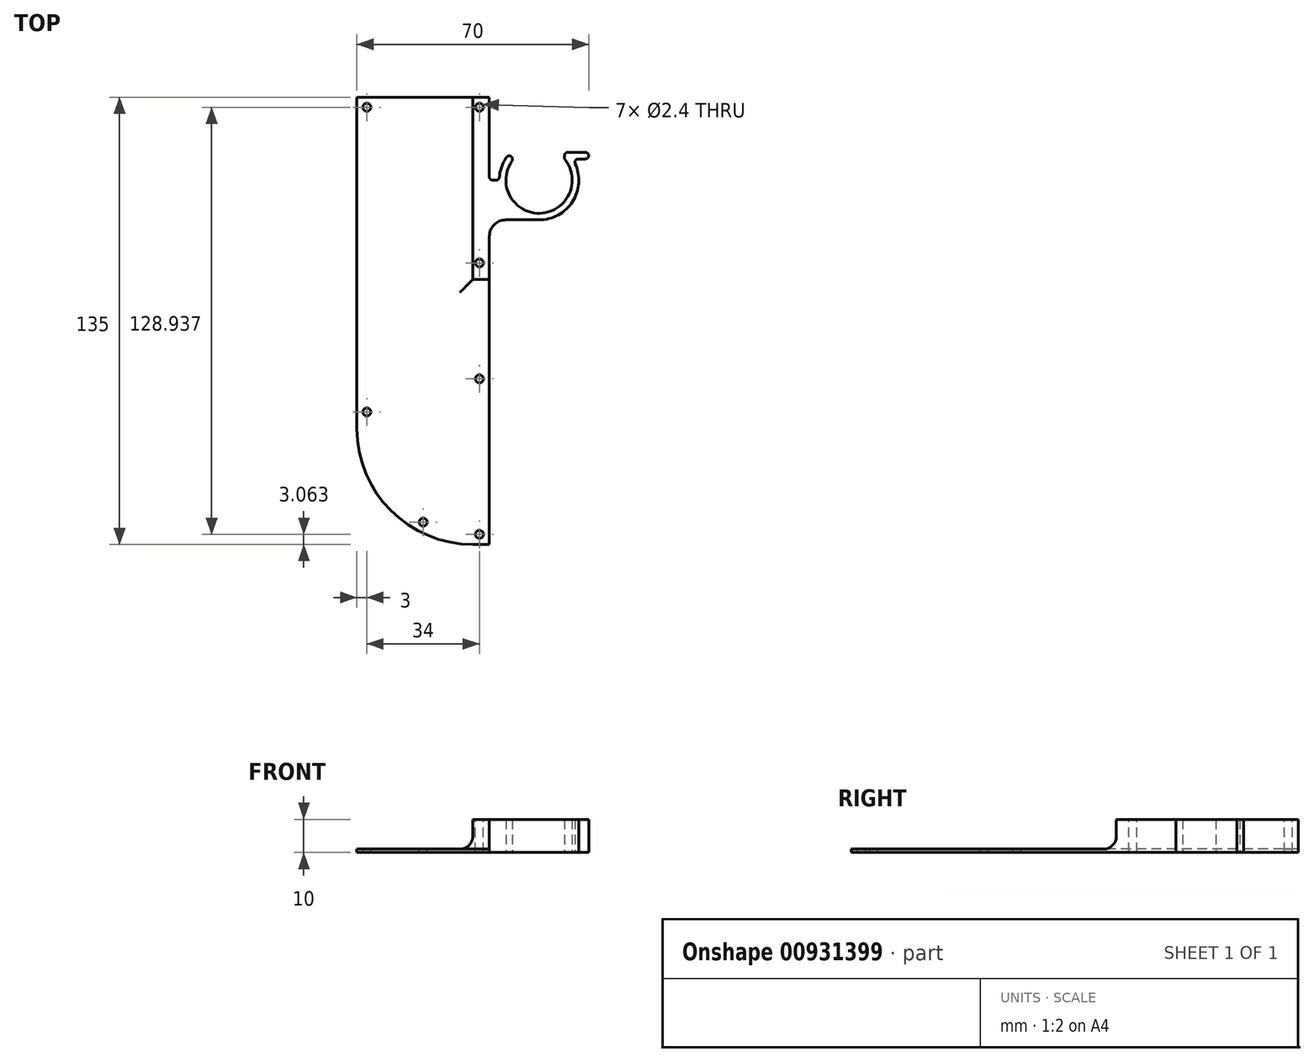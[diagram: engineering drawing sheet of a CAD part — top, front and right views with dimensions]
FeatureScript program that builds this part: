
annotation { "Feature Type Name" : "Feature", "Feature Type Description" : "" }
export const myFeature = defineFeature(function(context is Context, id is Id, definition is map)
    precondition{}
    {
        {
            var Q0;
            Q0=qCreatedBy(makeId("Top.planeOp"),FACE);
            var sketch = newSketch(context, id + "F0", { "sketchPlane" : qUnion([Q0])});
            skLineSegment(sketch, "E0.right", {"start": v(-70, 0) * mm, "end": v(-70, -100) * mm});
            skPoint(sketch, "E1.visualSharp", {"position": v(-70, -135) * mm});
            skArc(sketch, "E1.filletArc", {"start": v(-70, -100) * mm, "mid": v(-59.75, -124.75) * mm, "end": v(-35, -135) * mm});
            skArc(sketch, "E2", {"start": v(-23.18, -19.25) * mm, "mid": v(-14.76, -35) * mm, "end": v(-7.1, -18.86) * mm});
            skPoint(sketch, "E3.visualSharp", {"position": v(-23, -19) * mm});
            skPoint(sketch, "E0.top.start.orphan", {"position": v(0, -135) * mm});
            skPoint(sketch, "E4.visualSharp", {"position": v(-35, -45) * mm});
            skLineSegment(sketch, "E5", {"start": v(-35, -135) * mm, "end": v(-30, -135) * mm});
            skArc(sketch, "E6.0", {"start": v(-15, -37) * mm, "mid": v(-4.9, -31.49) * mm, "end": v(-4.08, -20.02) * mm});
            skLineSegment(sketch, "E7", {"start": v(-30, -135) * mm, "end": v(-30, -42) * mm});
            skLineSegment(sketch, "E8", {"start": v(-25, -37) * mm, "end": v(-15, -37) * mm});
            skPoint(sketch, "E8.endSnap0", {"position": v(-15, -37) * mm});
            skLineSegment(sketch, "E9", {"start": v(-70, 0) * mm, "end": v(-30, 0) * mm});
            skLineSegment(sketch, "E10", {"start": v(-7.18, -17.33) * mm, "end": v(-7.18, -17.33) * mm});
            skPoint(sketch, "E11.visualSharp", {"position": v(-7.86, -18) * mm});
            skPoint(sketch, "E12.visualSharp", {"position": v(-6.43, -16.6) * mm});
            skPoint(sketch, "E13.visualSharp", {"position": v(-30, -37) * mm});
            skArc(sketch, "E13.filletArc", {"start": v(-25, -37) * mm, "mid": v(-28.54, -38.46) * mm, "end": v(-30, -42) * mm});
            skArc(sketch, "E14.0", {"start": v(-24.82, -18.1) * mm, "mid": v(-26.3, -20.94) * mm, "end": v(-26.96, -24.08) * mm});
            skLineSegment(sketch, "E15.top", {"start": v(-27.96, -25) * mm, "end": v(-29, -25) * mm});
            skLineSegment(sketch, "E15.right", {"start": v(-30, 0) * mm, "end": v(-30, -24) * mm});
            skLineSegment(sketch, "E16", {"start": v(-23, -18.68) * mm, "end": v(-23, -18.68) * mm});
            skPoint(sketch, "E15.bottom.start.orphan", {"position": v(-23, 0) * mm});
            skPoint(sketch, "E17.visualSharp", {"position": v(-30, -25) * mm});
            skArc(sketch, "E17.filletArc", {"start": v(-30, -24) * mm, "mid": v(-29.7, -24.7) * mm, "end": v(-29, -25) * mm});
            skArc(sketch, "E18.filletArc", {"start": v(-27.96, -25) * mm, "mid": v(-27.28, -24.73) * mm, "end": v(-26.96, -24.08) * mm});
            skPoint(sketch, "E19.visualSharp", {"position": v(-23, -16.06) * mm});
            skArc(sketch, "E19.filletArc", {"start": v(-23, -18.68) * mm, "mid": v(-23.7, -17.72) * mm, "end": v(-24.82, -18.1) * mm});
            skArc(sketch, "E20.filletArc", {"start": v(-23.18, -19.25) * mm, "mid": v(-23.05, -18.98) * mm, "end": v(-23, -18.68) * mm});
            skLineSegment(sketch, "E21.bottom", {"start": v(-3.17, -18.6) * mm, "end": v(-1, -18.6) * mm});
            skLineSegment(sketch, "E21.top", {"start": v(-6.32, -16.6) * mm, "end": v(-1, -16.6) * mm});
            skLineSegment(sketch, "E21.left", {"start": v(-7.32, -18.25) * mm, "end": v(-7.32, -17.6) * mm});
            skLineSegment(sketch, "E21.right", {"start": v(0, -17.6) * mm, "end": v(0, -17.6) * mm});
            skPoint(sketch, "E22.visualSharp", {"position": v(-7.32, -16.6) * mm});
            skArc(sketch, "E22.filletArc", {"start": v(-6.32, -16.6) * mm, "mid": v(-7.02, -16.9) * mm, "end": v(-7.32, -17.6) * mm});
            skPoint(sketch, "E23.visualSharp", {"position": v(0, -16.6) * mm});
            skArc(sketch, "E23.filletArc", {"start": v(0, -17.6) * mm, "mid": v(-0.3, -16.9) * mm, "end": v(-1, -16.6) * mm});
            skPoint(sketch, "E24.visualSharp", {"position": v(0, -18.6) * mm});
            skArc(sketch, "E24.filletArc", {"start": v(-1, -18.6) * mm, "mid": v(-0.3, -18.3) * mm, "end": v(0, -17.6) * mm});
            skPoint(sketch, "E25.visualSharp", {"position": v(-4.85, -18.6) * mm});
            skArc(sketch, "E25.filletArc", {"start": v(-3.17, -18.6) * mm, "mid": v(-4.02, -19.06) * mm, "end": v(-4.08, -20.02) * mm});
            skPoint(sketch, "E26.visualSharp", {"position": v(-7.32, -18.6) * mm});
            skArc(sketch, "E26.filletArc", {"start": v(-7.32, -18.25) * mm, "mid": v(-7.26, -18.57) * mm, "end": v(-7.1, -18.86) * mm});
            skSolve(sketch);
        }
        {
            var Q0;
            Q0=makeQuery(id+"F0.imprint","IMPRINT",FACE,{"disambiguationData":[TD([[makeQuery(id+"F0.imprint","IMPRINT",EDGE,{"derivedFrom":sQuery(id+"F0.wireOp",EDGE,"E0.right")}),1.0]])]});
            extrude(context, id + "F1", {"entities" : qUnion([Q0]), "depth" : 10 * mm, "offsetDistance" : 25 * mm});
        }
        {
            var Q0;
            Q0=makeQuery(id+"F1.opExtrude","CAP_FACE",FACE,{"disambiguationData":[OSD([sQuery(id+"F0.wireOp",EDGE,"E0.top"),sQuery(id+"F0.wireOp",EDGE,"E0.left"),sQuery(id+"F0.wireOp",EDGE,"E0.right"),sQuery(id+"F0.wireOp",EDGE,"E1.filletArc"),sQuery(id+"F0.wireOp",EDGE,"5de082b1-88c5-4f56-9cd1-09331b00fd2d.trimOffspring"),sQuery(id+"F0.wireOp",EDGE,"E2"),sQuery(id+"F0.wireOp",EDGE,"uJFoRx8a-Ppp5-qDHF-xN9b-6GK6148I28lK.left"),sQuery(id+"F0.wireOp",EDGE,"uJFoRx8a-Ppp5-qDHF-xN9b-6GK6148I28lK.right"),sQuery(id+"F0.wireOp",EDGE,"b2af3c1e-7181-4fb0-8f65-0e7276eb82ca.trimOffspring"),sQuery(id+"F0.wireOp",EDGE,"7f23342a-69af-42d1-8bd4-2c05ba6568f0.filletArc"),sQuery(id+"F0.wireOp",EDGE,"185a892e-41b9-4107-83af-0d2bc894ce6d.filletArc"),sQuery(id+"F0.wireOp",EDGE,"b194760c-3b3b-4794-9b8b-2c71253df791.filletArc"),sQuery(id+"F0.wireOp",EDGE,"E3.filletArc"),sQuery(id+"F0.wireOp",EDGE,"ZXkUyEPo-FX4a-Sv19-M192-gNO29ZRSfF8I"),sQuery(id+"F0.wireOp",EDGE,"HvNRA3BX-9FXn-12fZ-Fs24-gRpAAjMtZzFk")])],"isStart":false});
            var sketch = newSketch(context, id + "F2", { "sketchPlane" : qUnion([Q0])});
            skLineSegment(sketch, "E27", {"start": v(-35, 0) * mm, "end": v(-70, 0) * mm});
            skLineSegment(sketch, "E28", {"start": v(-70, 0) * mm, "end": v(-70, -100) * mm});
            skLineSegment(sketch, "E29", {"start": v(-35, -135) * mm, "end": v(-30, -135) * mm});
            skLineSegment(sketch, "E30", {"start": v(-30, -135) * mm, "end": v(-30, -55) * mm});
            skLineSegment(sketch, "E31", {"start": v(-35, -135) * mm, "end": v(-35, -135) * mm});
            skLineSegment(sketch, "E32", {"start": v(-70, -100) * mm, "end": v(-70, -100) * mm});
            skPoint(sketch, "E33.visualSharp", {"position": v(-70, -135) * mm});
            skArc(sketch, "E33.filletArc", {"start": v(-70, -100) * mm, "mid": v(-59.75, -124.75) * mm, "end": v(-35, -135) * mm});
            skLineSegment(sketch, "E34.top", {"start": v(-30, -55) * mm, "end": v(-35, -55) * mm});
            skLineSegment(sketch, "E34.right", {"start": v(-35, 0) * mm, "end": v(-35, -55) * mm});
            skSolve(sketch);
        }
        {
            var Q0;
            Q0=makeQuery(id+"F2.imprint","IMPRINT",FACE,{"disambiguationData":[TD([[makeQuery(id+"F2.imprint","IMPRINT",EDGE,{"derivedFrom":sQuery(id+"F2.wireOp",EDGE,"ofFXBOQI-h16c-LmGf-cEx5-LxO6o4s5viPL")}),1.0]])]});
            var Q1;
            Q1=makeQuery(id+"F2.imprint","IMPRINT",FACE,{"disambiguationData":[TD([[makeQuery(id+"F2.imprint","IMPRINT",EDGE,{"derivedFrom":sQuery(id+"F2.wireOp",EDGE,"E27")}),-1.0]])]});
            extrude(context, id + "F3", {"entities" : qUnion([Q0, Q1]), "operationType" : NewBodyOperationType.REMOVE, "oppositeDirection" : true, "depth" : 9 * mm, "offsetDistance" : 25 * mm});
        }
        {
            var Q0;
            Q0=makeQuery(id+"F1.opExtrude","CAP_FACE",FACE,{"disambiguationData":[OSD([sQuery(id+"F0.wireOp",EDGE,"E0.top"),sQuery(id+"F0.wireOp",EDGE,"E0.left"),sQuery(id+"F0.wireOp",EDGE,"E0.right"),sQuery(id+"F0.wireOp",EDGE,"E1.filletArc"),sQuery(id+"F0.wireOp",EDGE,"5de082b1-88c5-4f56-9cd1-09331b00fd2d.trimOffspring"),sQuery(id+"F0.wireOp",EDGE,"E2"),sQuery(id+"F0.wireOp",EDGE,"uJFoRx8a-Ppp5-qDHF-xN9b-6GK6148I28lK.left"),sQuery(id+"F0.wireOp",EDGE,"uJFoRx8a-Ppp5-qDHF-xN9b-6GK6148I28lK.right"),sQuery(id+"F0.wireOp",EDGE,"b2af3c1e-7181-4fb0-8f65-0e7276eb82ca.trimOffspring"),sQuery(id+"F0.wireOp",EDGE,"7f23342a-69af-42d1-8bd4-2c05ba6568f0.filletArc"),sQuery(id+"F0.wireOp",EDGE,"185a892e-41b9-4107-83af-0d2bc894ce6d.filletArc"),sQuery(id+"F0.wireOp",EDGE,"b194760c-3b3b-4794-9b8b-2c71253df791.filletArc"),sQuery(id+"F0.wireOp",EDGE,"E3.filletArc"),sQuery(id+"F0.wireOp",EDGE,"ZXkUyEPo-FX4a-Sv19-M192-gNO29ZRSfF8I"),sQuery(id+"F0.wireOp",EDGE,"HvNRA3BX-9FXn-12fZ-Fs24-gRpAAjMtZzFk")])],"isStart":false});
            var sketch = newSketch(context, id + "F4", { "sketchPlane" : qUnion([Q0])});
            skArc(sketch, "E35.1", {"start": v(-67, -100) * mm, "mid": v(-57.63, -122.63) * mm, "end": v(-35, -132) * mm, "construction": true});
            skLineSegment(sketch, "E35.2", {"start": v(-67, 0) * mm, "end": v(-67, -100) * mm, "construction": true});
            skPoint(sketch, "E36", {"position": v(-67, -3) * mm});
            skPoint(sketch, "E37", {"position": v(-50, -128.27) * mm});
            skPoint(sketch, "E38", {"position": v(-33, -131.94) * mm});
            skLineSegment(sketch, "E39.0", {"start": v(-33, 0) * mm, "end": v(-33, -135) * mm, "construction": true});
            skPoint(sketch, "E40", {"position": v(-33, -85) * mm});
            skPoint(sketch, "E41", {"position": v(-33, -50) * mm});
            skPoint(sketch, "E42", {"position": v(-33, -3) * mm});
            skPoint(sketch, "E43", {"position": v(-67, -95) * mm});
            skSolve(sketch);
        }
        {
            var Q0;
            Q0=sQuery(id+"F4.wireOp",VERTEX,"E36");
            var Q1;
            Q1=sQuery(id+"F4.wireOp",VERTEX,"f4559d67-b2ce-4cbe-8c48-f7303b728956.direction1.end");
            var Q2;
            Q2=sQuery(id+"F4.wireOp",VERTEX,"666fff49-049b-4152-8810-0d37dc0279b3");
            var Q3;
            Q3=sQuery(id+"F4.wireOp",VERTEX,"E37");
            var Q4;
            Q4=sQuery(id+"F4.wireOp",VERTEX,"E38");
            var Q5;
            Q5=sQuery(id+"F4.wireOp",VERTEX,"E40");
            var Q6;
            Q6=sQuery(id+"F4.wireOp",VERTEX,"E41");
            var Q7;
            Q7=sQuery(id+"F4.wireOp",VERTEX,"E42");
            var Q8;
            Q8=sQuery(id+"F4.wireOp",VERTEX,"E43");
            var Q9;
            Q9=makeQuery(id+"F1.opExtrude","SWEPT_BODY",BODY,{"disambiguationData":[OSD([sQuery(id+"F0.wireOp",EDGE,"E0.top"),sQuery(id+"F0.wireOp",EDGE,"E0.left"),sQuery(id+"F0.wireOp",EDGE,"E0.right"),sQuery(id+"F0.wireOp",EDGE,"E1.filletArc"),sQuery(id+"F0.wireOp",EDGE,"5de082b1-88c5-4f56-9cd1-09331b00fd2d.trimOffspring"),sQuery(id+"F0.wireOp",EDGE,"E2"),sQuery(id+"F0.wireOp",EDGE,"uJFoRx8a-Ppp5-qDHF-xN9b-6GK6148I28lK.left"),sQuery(id+"F0.wireOp",EDGE,"uJFoRx8a-Ppp5-qDHF-xN9b-6GK6148I28lK.right"),sQuery(id+"F0.wireOp",EDGE,"b2af3c1e-7181-4fb0-8f65-0e7276eb82ca.trimOffspring"),sQuery(id+"F0.wireOp",EDGE,"7f23342a-69af-42d1-8bd4-2c05ba6568f0.filletArc"),sQuery(id+"F0.wireOp",EDGE,"185a892e-41b9-4107-83af-0d2bc894ce6d.filletArc"),sQuery(id+"F0.wireOp",EDGE,"b194760c-3b3b-4794-9b8b-2c71253df791.filletArc"),sQuery(id+"F0.wireOp",EDGE,"E3.filletArc"),sQuery(id+"F0.wireOp",EDGE,"ZXkUyEPo-FX4a-Sv19-M192-gNO29ZRSfF8I"),sQuery(id+"F0.wireOp",EDGE,"HvNRA3BX-9FXn-12fZ-Fs24-gRpAAjMtZzFk")])]});
            hole(context, id + "F5", {"style" : HoleStyle.SIMPLE, "endStyle" : HoleEndStyle.THROUGH, "holeDiameter" : 2.4 * mm, "majorDiameter" : 5 * mm, "isTappedThrough" : true, "tappedDepth" : 12 * mm, "tapClearance" : 3, "locations" : qUnion([Q0, Q1, Q2, Q3, Q4, Q5, Q6, Q7, Q8]), "scope" : qUnion([Q9])});
        }
        {
            var Q0;
            Q0=makeQuery(id+"F3.boolean.opBoolean","COPY",EDGE,{"derivedFrom":makeQuery(id+"F3.opExtrude","CAP_EDGE",EDGE,{"disambiguationData":[OSD([sQuery(id+"F2.wireOp",EDGE,"E34.right")])],"isStart":false})});
            var Q1;
            Q1=makeQuery(id+"F3.boolean.opBoolean","COPY",EDGE,{"derivedFrom":makeQuery(id+"F3.opExtrude","CAP_EDGE",EDGE,{"disambiguationData":[OSD([sQuery(id+"F2.wireOp",EDGE,"E34.top")])],"isStart":false})});
            var Q2;
            Q2=makeQuery(id+"F3.boolean.opBoolean","COPY",EDGE,{"derivedFrom":makeQuery(id+"F3.opExtrude","CAP_EDGE",EDGE,{"disambiguationData":[OSD([sQuery(id+"F2.wireOp",EDGE,"E34.top")])],"isStart":true})});
            var Q3;
            Q3=makeQuery(id+"F3.boolean.opBoolean","COPY",EDGE,{"derivedFrom":makeQuery(id+"F3.opExtrude","CAP_EDGE",EDGE,{"disambiguationData":[OSD([sQuery(id+"F2.wireOp",EDGE,"E34.right")])],"isStart":true})});
            fillet(context, id + "F6", {"entities" : qUnion([Q0, Q1, Q2, Q3]), "radius" : 3.9 * mm, "tangentPropagation" : true, "allowEdgeOverflow" : false});
        }
    });
